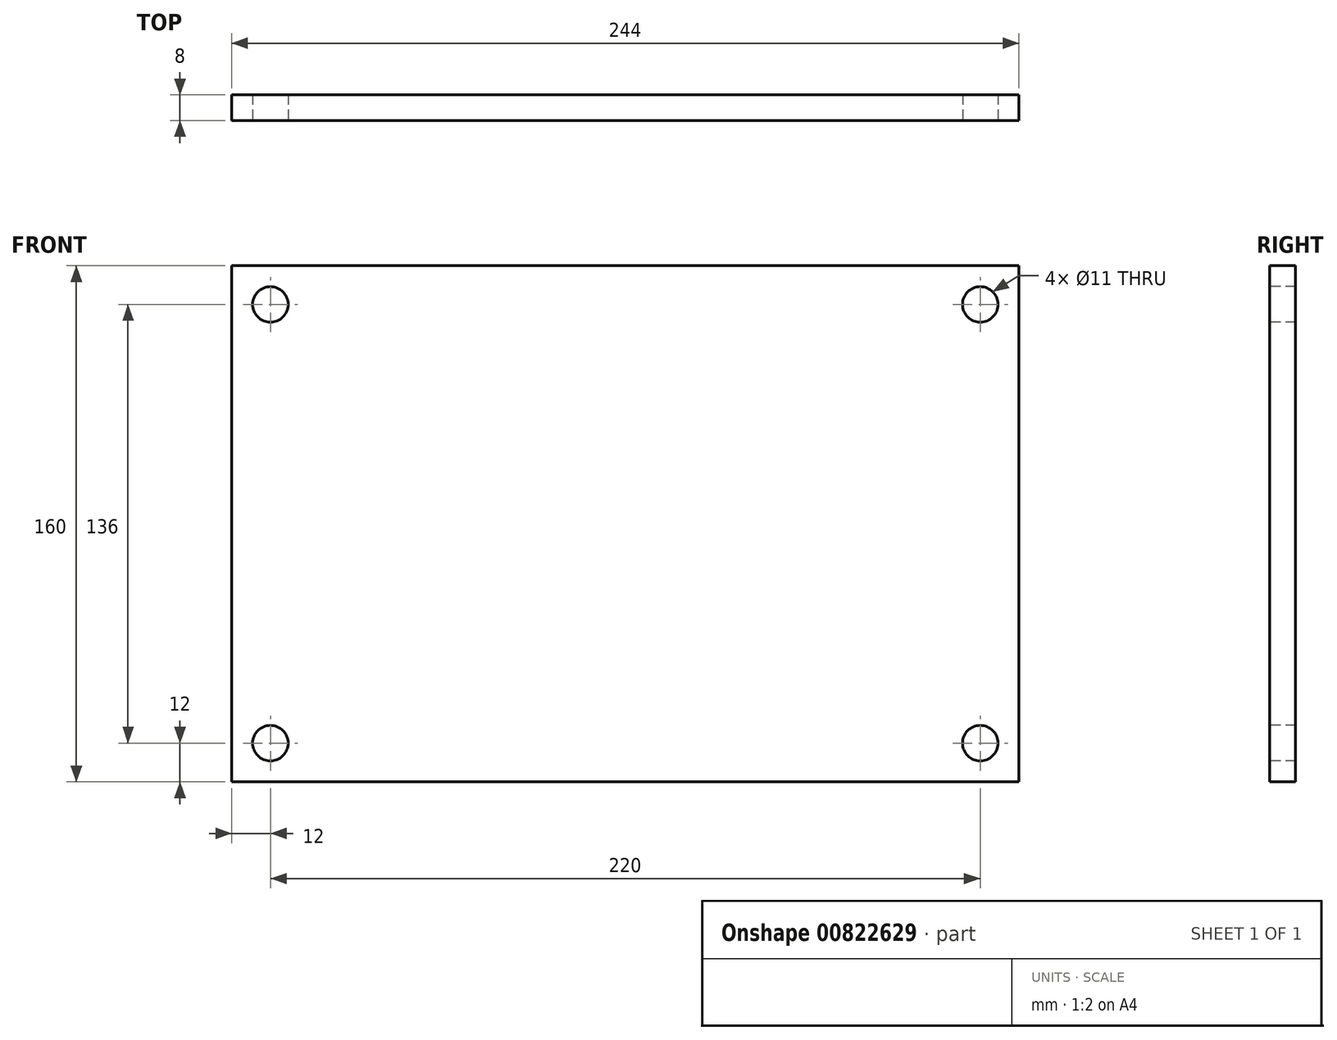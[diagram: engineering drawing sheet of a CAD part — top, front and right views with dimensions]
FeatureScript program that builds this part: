
annotation { "Feature Type Name" : "Feature", "Feature Type Description" : "" }
export const myFeature = defineFeature(function(context is Context, id is Id, definition is map)
    precondition{}
    {
        {
            var Q0;
            Q0=qCreatedBy(makeId("Front.planeOp"),FACE);
            var sketch = newSketch(context, id + "F0", { "sketchPlane" : qUnion([Q0])});
            skLineSegment(sketch, "E0.bottom", {"start": v(-122, 80) * mm, "end": v(122, 80) * mm});
            skLineSegment(sketch, "E0.top", {"start": v(-122, -80) * mm, "end": v(122, -80) * mm});
            skLineSegment(sketch, "E0.left", {"start": v(-122, 80) * mm, "end": v(-122, -80) * mm});
            skLineSegment(sketch, "E0.right", {"start": v(122, 80) * mm, "end": v(122, -80) * mm});
            skPoint(sketch, "E0.middle", {"position": v(0, 0) * mm});
            skSolve(sketch);
        }
        {
            var Q0;
            Q0=makeQuery(id+"F0.imprint","IMPRINT",FACE,{"disambiguationData":[TD([[makeQuery(id+"F0.imprint","IMPRINT",EDGE,{"derivedFrom":sQuery(id+"F0.wireOp",EDGE,"E0.bottom")}),-1.0]])]});
            extrude(context, id + "F1", {"entities" : qUnion([Q0]), "depth" : 8 * mm, "offsetDistance" : 25 * mm, "symmetric" : true});
        }
        {
            var Q0;
            Q0=makeQuery(id+"F1.opExtrude","CAP_FACE",FACE,{"disambiguationData":[OSD([sQuery(id+"F0.wireOp",EDGE,"E0.bottom"),sQuery(id+"F0.wireOp",EDGE,"E0.top"),sQuery(id+"F0.wireOp",EDGE,"E0.left"),sQuery(id+"F0.wireOp",EDGE,"E0.right")])],"isStart":false});
            var sketch = newSketch(context, id + "F2", { "sketchPlane" : qUnion([Q0])});
            skLineSegment(sketch, "E1.bottom", {"start": v(-110, 68) * mm, "end": v(110, 68) * mm});
            skLineSegment(sketch, "E1.top", {"start": v(-110, -68) * mm, "end": v(110, -68) * mm});
            skLineSegment(sketch, "E1.left", {"start": v(-110, 68) * mm, "end": v(-110, -68) * mm});
            skLineSegment(sketch, "E1.right", {"start": v(110, 68) * mm, "end": v(110, -68) * mm});
            skPoint(sketch, "E1.middle", {"position": v(0, 0) * mm});
            skSolve(sketch);
        }
        {
            var Q0;
            Q0=sQuery(id+"F2.wireOp",VERTEX,"E1.bottom.end");
            var Q1;
            Q1=sQuery(id+"F2.wireOp",VERTEX,"E1.top.end");
            var Q2;
            Q2=sQuery(id+"F2.wireOp",VERTEX,"E1.top.start");
            var Q3;
            Q3=sQuery(id+"F2.wireOp",VERTEX,"E1.bottom.start");
            var Q4;
            Q4=makeQuery(id+"F1.opExtrude","SWEPT_BODY",BODY,{"disambiguationData":[OSD([sQuery(id+"F0.wireOp",EDGE,"E0.bottom"),sQuery(id+"F0.wireOp",EDGE,"E0.top"),sQuery(id+"F0.wireOp",EDGE,"E0.left"),sQuery(id+"F0.wireOp",EDGE,"E0.right")])]});
            hole(context, id + "F3", {"style" : HoleStyle.SIMPLE, "endStyle" : HoleEndStyle.THROUGH, "holeDiameter" : 11 * mm, "majorDiameter" : 5 * mm, "isTappedThrough" : true, "tappedDepth" : 12 * mm, "tapClearance" : 3, "locations" : qUnion([Q0, Q1, Q2, Q3]), "scope" : qUnion([Q4])});
        }
    });
